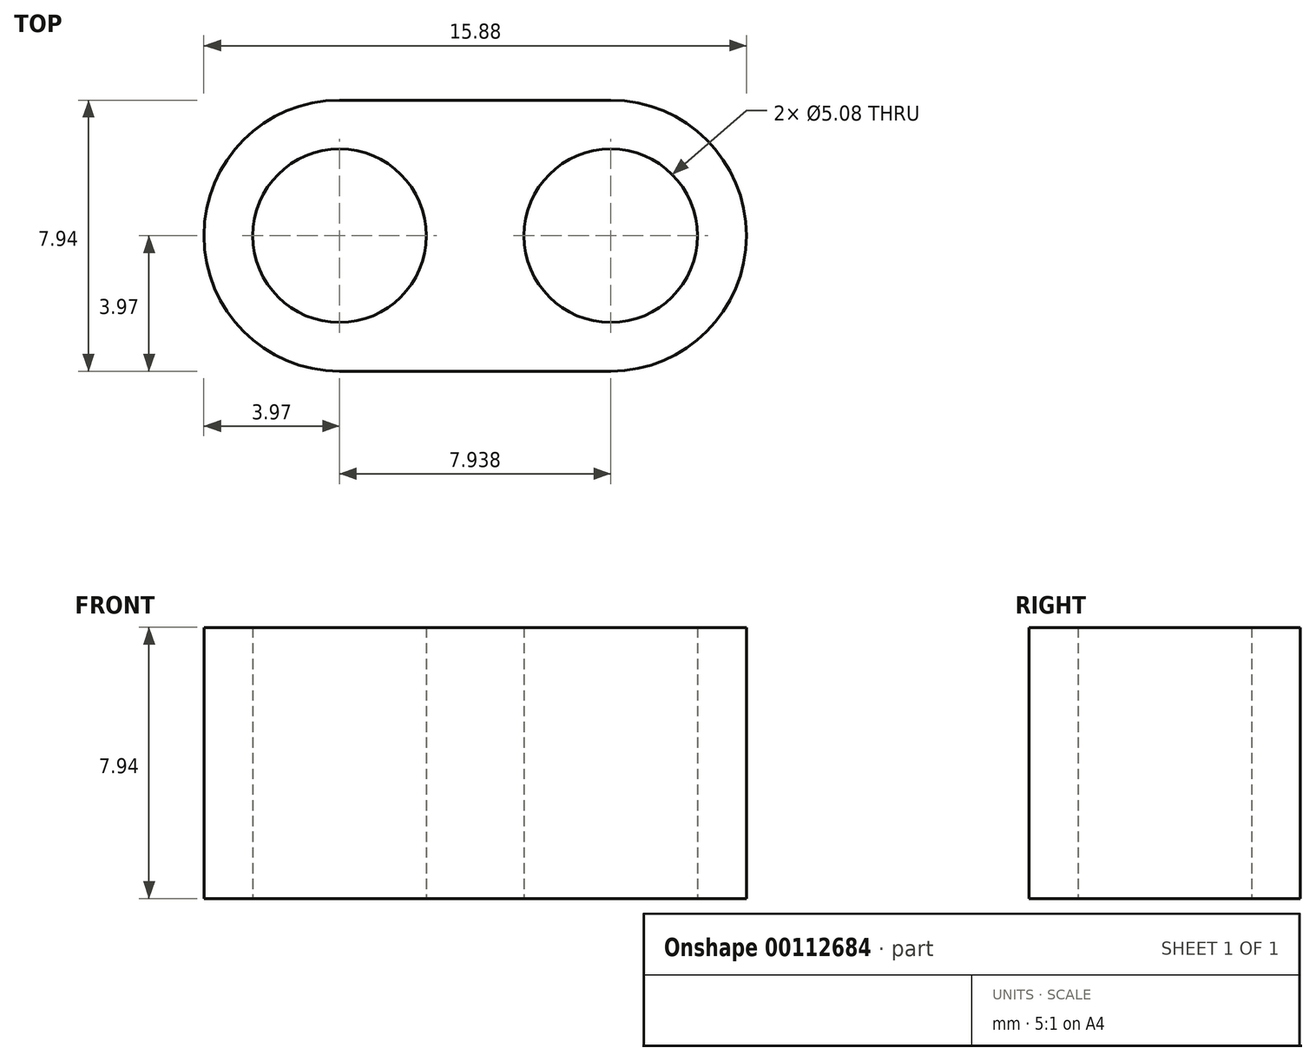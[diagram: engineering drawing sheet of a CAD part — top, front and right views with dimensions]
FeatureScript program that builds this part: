
annotation { "Feature Type Name" : "Feature", "Feature Type Description" : "" }
export const myFeature = defineFeature(function(context is Context, id is Id, definition is map)
    precondition{}
    {
        {
            var Q0;
            Q0=qCreatedBy(makeId("Top.planeOp"),FACE);
            var sketch = newSketch(context, id + "F0", { "sketchPlane" : qUnion([Q0])});
            skLineSegment(sketch, "E0", {"start": v(0, 0) * mm, "end": v(7.94, 0) * mm, "construction": true});
            skLineSegment(sketch, "E1.bottom", {"start": v(0, 3.97) * mm, "end": v(7.94, 3.97) * mm});
            skLineSegment(sketch, "E1.top", {"start": v(0, -3.97) * mm, "end": v(7.94, -3.97) * mm});
            skLineSegment(sketch, "E1.left", {"start": v(0, 3.97) * mm, "end": v(0, -3.97) * mm});
            skLineSegment(sketch, "E1.right", {"start": v(7.94, 3.97) * mm, "end": v(7.94, -3.97) * mm});
            skArc(sketch, "E2", {"start": v(0, 3.97) * mm, "mid": v(-3.97, 0) * mm, "end": v(0, -3.97) * mm});
            skArc(sketch, "E3", {"start": v(7.94, -3.97) * mm, "mid": v(11.9, 0) * mm, "end": v(7.94, 3.97) * mm});
            skCircle(sketch, "E4", {"center": v(0, 0) * mm, "radius": 2.54 * mm});
            skCircle(sketch, "E5", {"center": v(7.94, 0) * mm, "radius": 2.54 * mm});
            skSolve(sketch);
        }
        {
            var Q0;
            Q0=qSketchRegion(id+"F0",true);
            extrude(context, id + "F1", {"entities" : qUnion([Q0]), "depth" : 7.94 * mm});
        }
    });
